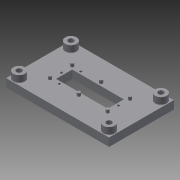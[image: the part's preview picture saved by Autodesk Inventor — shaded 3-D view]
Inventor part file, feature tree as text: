
AUTODESK INVENTOR PART (.ipt)
format: ipt  version: 2015 (Build 190159000, 159)  size: 168,448 bytes
history: native  units: in
note: dims shown in document units (in); Inventor stores cm internally (conversion verified against a paired STEP export)
features: extrude x4, sketch x2
ambient origin geometry x8: Origin, YZ Plane, XZ Plane, XY Plane, X Axis, Y Axis, Z Axis, Center Point
bodies: Solid1 (feature_tree)
feature tree (6):
  extrude  "Extrusion1"  Depth=2.6575in
  extrude  "Extrusion2"  Depth=0.0394in
  extrude  "Extrusion4"  Depth=0.0394in
  extrude  "Extrusion5"  Depth=0.0394in
  sketch  "Sketch1"  dims[d0=1.6732in d1=2.6575in]
  sketch  "Sketch5"  dims[d2=0.2091in d3=0.0in d4=0.0591in d15=0.5535in d23=1.4701in d31=0.1181in d32=0.0in d39=0.2217in d59=0.0787in d60=0.0in d69=0.1181in d70=0.1673in d79=0.1378in d90=0.1673in d91=0.1673in d92=0.0787in d93=1.3386in d94=2.3228in d95=0.0787in d96=0.0787in d97=0.0787in d98=0.0906in d99=0.0in d101=0.0394in d102=0.0394in d103=0.0394in d105=0.0394in]
